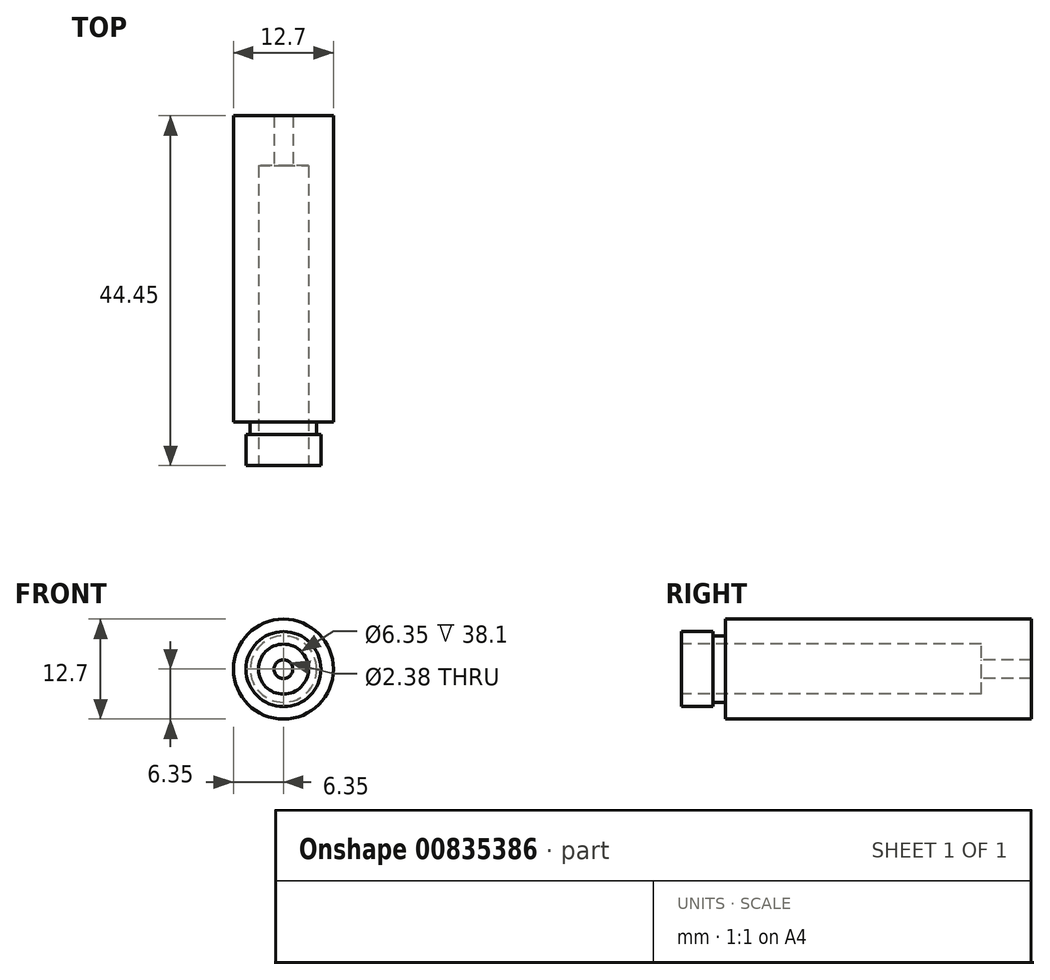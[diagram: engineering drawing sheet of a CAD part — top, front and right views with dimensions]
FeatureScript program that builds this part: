
annotation { "Feature Type Name" : "Feature", "Feature Type Description" : "" }
export const myFeature = defineFeature(function(context is Context, id is Id, definition is map)
    precondition{}
    {
        {
            var Q0;
            Q0=qCreatedBy(makeId("Top.planeOp"),FACE);
            var sketch = newSketch(context, id + "F0", { "sketchPlane" : qUnion([Q0])});
            skLineSegment(sketch, "E0", {"start": v(3.18, 0) * mm, "end": v(4.76, 0) * mm});
            skLineSegment(sketch, "E1", {"start": v(4.76, 0) * mm, "end": v(4.76, 3.97) * mm});
            skLineSegment(sketch, "E2", {"start": v(4.76, 3.97) * mm, "end": v(4.22, 3.97) * mm});
            skLineSegment(sketch, "E3", {"start": v(4.22, 3.97) * mm, "end": v(4.22, 5.56) * mm});
            skLineSegment(sketch, "E4", {"start": v(4.22, 5.56) * mm, "end": v(6.35, 5.56) * mm});
            skLineSegment(sketch, "E5", {"start": v(6.35, 5.56) * mm, "end": v(6.35, 44.45) * mm});
            skLineSegment(sketch, "E6", {"start": v(6.35, 44.45) * mm, "end": v(1.2, 44.45) * mm});
            skLineSegment(sketch, "E7", {"start": v(1.2, 44.45) * mm, "end": v(1.2, 38.1) * mm});
            skLineSegment(sketch, "E8", {"start": v(3.17, 38.1) * mm, "end": v(1.2, 38.1) * mm});
            skLineSegment(sketch, "E9", {"start": v(3.17, 38.1) * mm, "end": v(3.18, 0) * mm});
            skLineSegment(sketch, "E10", {"start": v(-3.18, 0) * mm, "end": v(-3.17, 38.1) * mm});
            skLineSegment(sketch, "E11", {"start": v(-3.17, 38.1) * mm, "end": v(-1.2, 38.1) * mm});
            skLineSegment(sketch, "E12", {"start": v(-1.2, 38.1) * mm, "end": v(-1.2, 44.45) * mm});
            skLineSegment(sketch, "E13", {"start": v(-1.2, 44.45) * mm, "end": v(-6.35, 44.45) * mm});
            skLineSegment(sketch, "E14", {"start": v(-6.35, 44.45) * mm, "end": v(-6.35, 5.56) * mm});
            skLineSegment(sketch, "E15", {"start": v(-6.35, 5.56) * mm, "end": v(-4.22, 5.56) * mm});
            skLineSegment(sketch, "E16", {"start": v(-4.22, 5.56) * mm, "end": v(-4.22, 3.97) * mm});
            skLineSegment(sketch, "E17", {"start": v(-4.22, 3.97) * mm, "end": v(-4.76, 3.97) * mm});
            skLineSegment(sketch, "E18", {"start": v(-4.76, 3.97) * mm, "end": v(-4.76, 0) * mm});
            skLineSegment(sketch, "E19", {"start": v(-4.76, 0) * mm, "end": v(-3.18, 0) * mm});
            skLineSegment(sketch, "E20", {"start": v(0, 0) * mm, "end": v(0, 44.45) * mm, "construction": true});
            skSolve(sketch);
        }
        {
            var Q0;
            Q0=makeQuery(id+"F0.imprint","IMPRINT",FACE,{"disambiguationData":[TD([[makeQuery(id+"F0.imprint","IMPRINT",EDGE,{"derivedFrom":sQuery(id+"F0.wireOp",EDGE,"E0")}),1.0]])]});
            var Q1;
            Q1=sQuery(id+"F0.wireOp",EDGE,"E20");
            revolve(context, id + "F1", {"surfaceOperationType" : NewSurfaceOperationType.NEW, "entities" : qUnion([Q0]), "axis" : qUnion([Q1]), "revolveType" : RevolveType.FULL});
        }
    });
